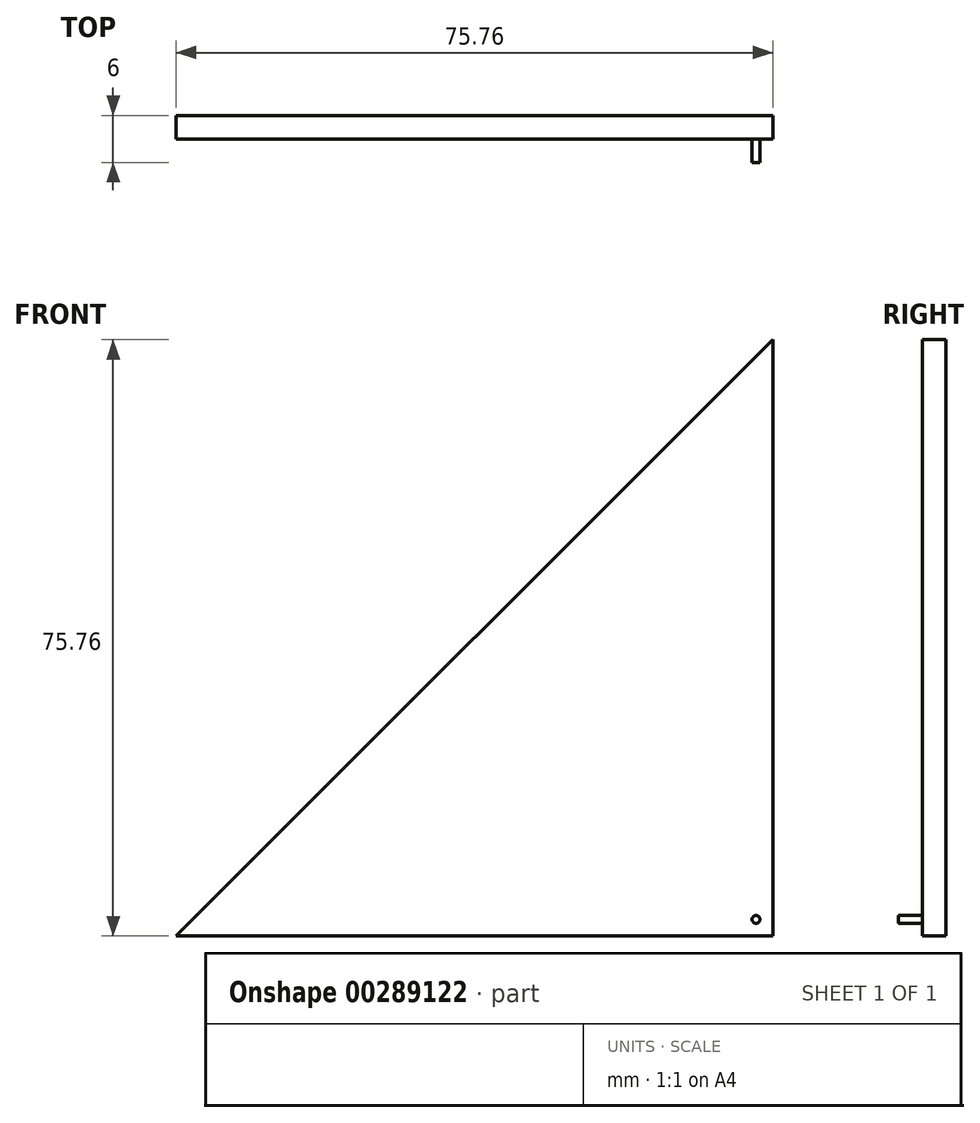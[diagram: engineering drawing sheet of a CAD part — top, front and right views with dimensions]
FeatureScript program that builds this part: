
annotation { "Feature Type Name" : "Feature", "Feature Type Description" : "" }
export const myFeature = defineFeature(function(context is Context, id is Id, definition is map)
    precondition{}
    {
        {
            var Q0;
            Q0=qCreatedBy(makeId("Front.planeOp"),FACE);
            var sketch = newSketch(context, id + "F0", { "sketchPlane" : qUnion([Q0])});
            skLineSegment(sketch, "E0.bottom", {"start": v(40, -40) * mm, "end": v(-40, -40) * mm, "construction": true});
            skLineSegment(sketch, "E0.top", {"start": v(40, 40) * mm, "end": v(-40, 40) * mm, "construction": true});
            skLineSegment(sketch, "E0.left", {"start": v(40, -40) * mm, "end": v(40, 40) * mm, "construction": true});
            skLineSegment(sketch, "E0.right", {"start": v(-40, -40) * mm, "end": v(-40, 40) * mm, "construction": true});
            skPoint(sketch, "E0.middle", {"position": v(0, 0) * mm});
            skLineSegment(sketch, "E1", {"start": v(40, 40) * mm, "end": v(-40, -40) * mm, "construction": true});
            skLineSegment(sketch, "E2", {"start": v(40, -40) * mm, "end": v(-35.76, -40) * mm});
            skLineSegment(sketch, "E3", {"start": v(-35.76, -40) * mm, "end": v(40, 35.76) * mm});
            skLineSegment(sketch, "E4", {"start": v(40, 35.76) * mm, "end": v(40, -40) * mm});
            skLineSegment(sketch, "E5", {"start": v(40, -40) * mm, "end": v(2.12, -2.12) * mm, "construction": true});
            skCircle(sketch, "E6", {"center": v(37.88, -37.88) * mm, "radius": 0.5 * mm});
            skSolve(sketch);
        }
        {
            var Q0;
            Q0=makeQuery(id+"F0.imprint","IMPRINT",FACE,{"disambiguationData":[TD([[makeQuery(id+"F0.imprint","IMPRINT",EDGE,{"derivedFrom":sQuery(id+"F0.wireOp",EDGE,"E2")}),-1.0]])]});
            extrude(context, id + "F1", {"entities" : qUnion([Q0]), "depth" : 3 * mm});
        }
        {
            var Q0;
            Q0=makeQuery(id+"F0.imprint","IMPRINT",FACE,{"disambiguationData":[TD([[makeQuery(id+"F0.imprint","IMPRINT",EDGE,{"derivedFrom":sQuery(id+"F0.wireOp",EDGE,"E6")}),1.0]])]});
            extrude(context, id + "F2", {"entities" : qUnion([Q0]), "operationType" : NewBodyOperationType.ADD, "depth" : 6 * mm});
        }
    });
